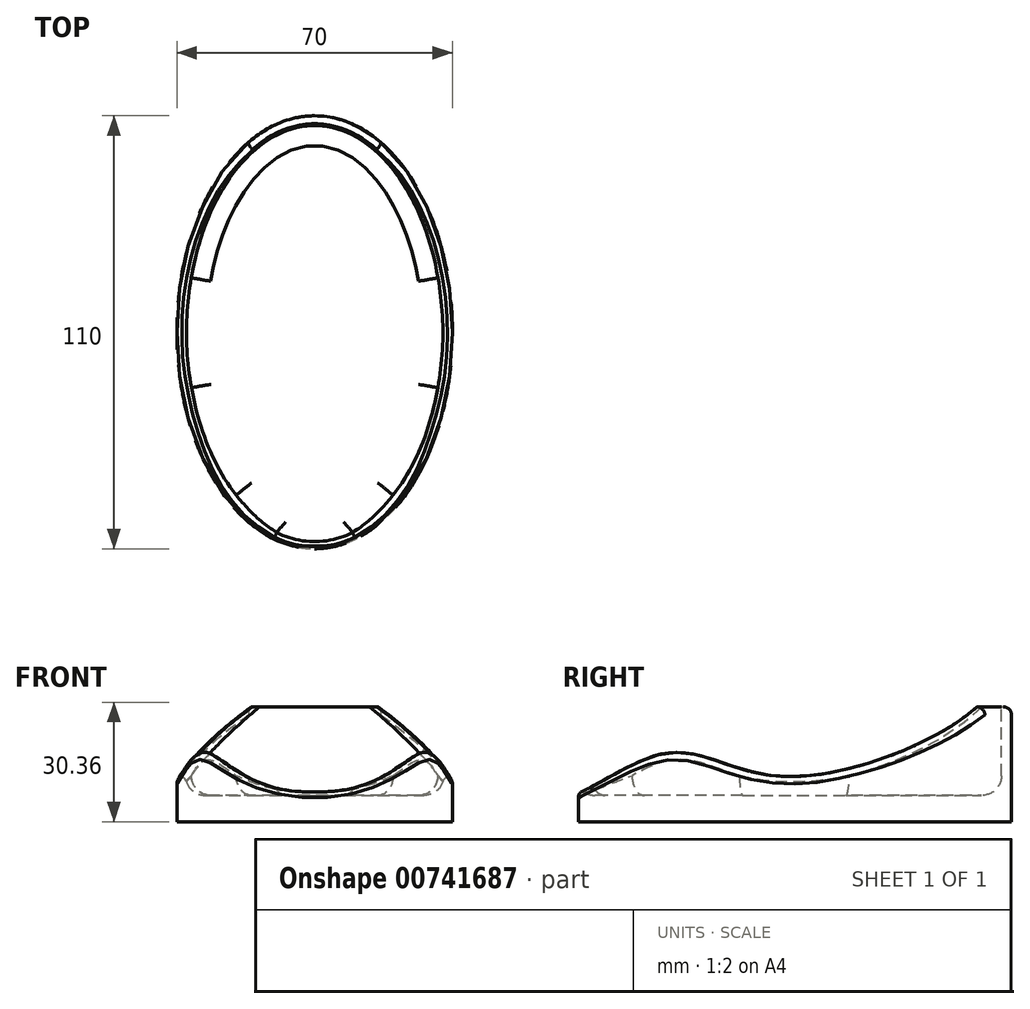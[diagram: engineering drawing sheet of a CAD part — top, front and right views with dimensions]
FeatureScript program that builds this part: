
annotation { "Feature Type Name" : "Feature", "Feature Type Description" : "" }
export const myFeature = defineFeature(function(context is Context, id is Id, definition is map)
    precondition{}
    {
        {
            var Q0;
            Q0=qCreatedBy(makeId("Top.planeOp"),FACE);
            var sketch = newSketch(context, id + "F0", { "sketchPlane" : qUnion([Q0])});
            skEllipse(sketch, "E0", {"center": v(0, 0) * mm, "majorRadius": 35 * mm, "minorRadius": 55 * mm, "majorAxis": v(1, 0)});
            skLineSegment(sketch, "E1", {"start": v(0, 61.16) * mm, "end": v(0, -65.82) * mm, "construction": true});
            skSolve(sketch);
        }
        {
            var Q0;
            Q0=makeQuery(id+"F0.imprint","IMPRINT",FACE,{"disambiguationData":[TD([[makeQuery(id+"F0.imprint","IMPRINT",EDGE,{"derivedFrom":sQuery(id+"F0.wireOp",EDGE,"E0")}),1.0]])]});
            extrude(context, id + "F1", {"entities" : qUnion([Q0]), "depth" : 25 * mm, "offsetDistance" : 25 * mm});
        }
        {
            var Q0;
            Q0=makeQuery(id+"F1.opExtrude","CAP_FACE",FACE,{"disambiguationData":[OSD([sQuery(id+"F0.wireOp",EDGE,"E0")])],"isStart":false});
            shell(context, id + "F2", {"entities" : qUnion([Q0]), "thickness" : 2.5 * mm});
        }
        {
            var Q0;
            Q0=qCreatedBy(makeId("Right.planeOp"),FACE);
            var sketch = newSketch(context, id + "F3", { "sketchPlane" : qUnion([Q0])});
            skFitSpline(sketch, "E2", {"points": [v(52.05, 38.67) * mm, v(0, 7.41) * mm, v(-33.68, 13.21) * mm, v(-73.64, 0) * mm, v(-74.93, 52.86) * mm, v(52.05, 38.67) * mm]});
            skSolve(sketch);
        }
        {
            var Q0;
            Q0 = qSketchRegion(id + "F3", true);
            extrude(context, id + "F4", {"entities" : qUnion([Q0]), "operationType" : NewBodyOperationType.REMOVE, "endBound" : BoundingType.SYMMETRIC, "oppositeDirection" : true, "depth" : 100 * mm, "offsetDistance" : 25 * mm});
        }
        {
            var Q0;
            {var subQ0=sQuery(id+"F0.wireOp",EDGE,"E0");Q0=makeQuery(id+"F4.boolean.opBoolean","INTERSECT",EDGE,{"derivedFrom":[makeQuery(id+"F2.opShell","OFFSET_FACE",FACE,{"disambiguationData":[OSD([subQ0]),TDD([makeQuery(id+"F1.opExtrude","SWEPT_FACE",FACE,{"disambiguationData":[OSD([subQ0])]})])]}),makeQuery(id+"F4.opExtrude","SWEPT_FACE",FACE,{"disambiguationData":[OSD([sQuery(id+"F3.wireOp",EDGE,"E2")])]})]});}
            var Q1;
            Q1=makeQuery(id+"F4.boolean.opBoolean","INTERSECT",EDGE,{"derivedFrom":[makeQuery(id+"F1.opExtrude","SWEPT_FACE",FACE,{"disambiguationData":[OSD([sQuery(id+"F0.wireOp",EDGE,"E0")])]}),makeQuery(id+"F4.opExtrude","SWEPT_FACE",FACE,{"disambiguationData":[OSD([sQuery(id+"F3.wireOp",EDGE,"E2")])]})]});
            var Q2;
            Q2=makeQuery(id+"F1.opExtrude","CAP_EDGE",EDGE,{"disambiguationData":[OSD([sQuery(id+"F0.wireOp",EDGE,"E0")])],"isStart":false});
            fillet(context, id + "F5", {"entities" : qUnion([Q0, Q1, Q2]), "radius" : 2 * mm, "tangentPropagation" : true, "allowEdgeOverflow" : false});
        }
        {
            var Q0;
            Q0=makeQuery(id+"F1.opExtrude","CAP_FACE",FACE,{"disambiguationData":[OSD([sQuery(id+"F0.wireOp",EDGE,"E0")])],"isStart":true});
            extrude(context, id + "F6", {"entities" : qUnion([Q0]), "operationType" : NewBodyOperationType.ADD, "depth" : 4.2 * mm, "offsetDistance" : 25 * mm});
        }
        {
            var Q0;
            {var subQ0=sQuery(id+"F0.wireOp",EDGE,"E0");Q0=makeQuery(id+"F2.opShell","OFFSET_EDGE",EDGE,{"disambiguationData":[OSD([subQ0]),TDD([makeQuery(id+"F1.opExtrude","CAP_EDGE",EDGE,{"disambiguationData":[OSD([subQ0])],"isStart":true})])]});}
            fillet(context, id + "F7", {"entities" : qUnion([Q0]), "radius" : 5 * mm, "tangentPropagation" : true, "allowEdgeOverflow" : false});
        }
    });
